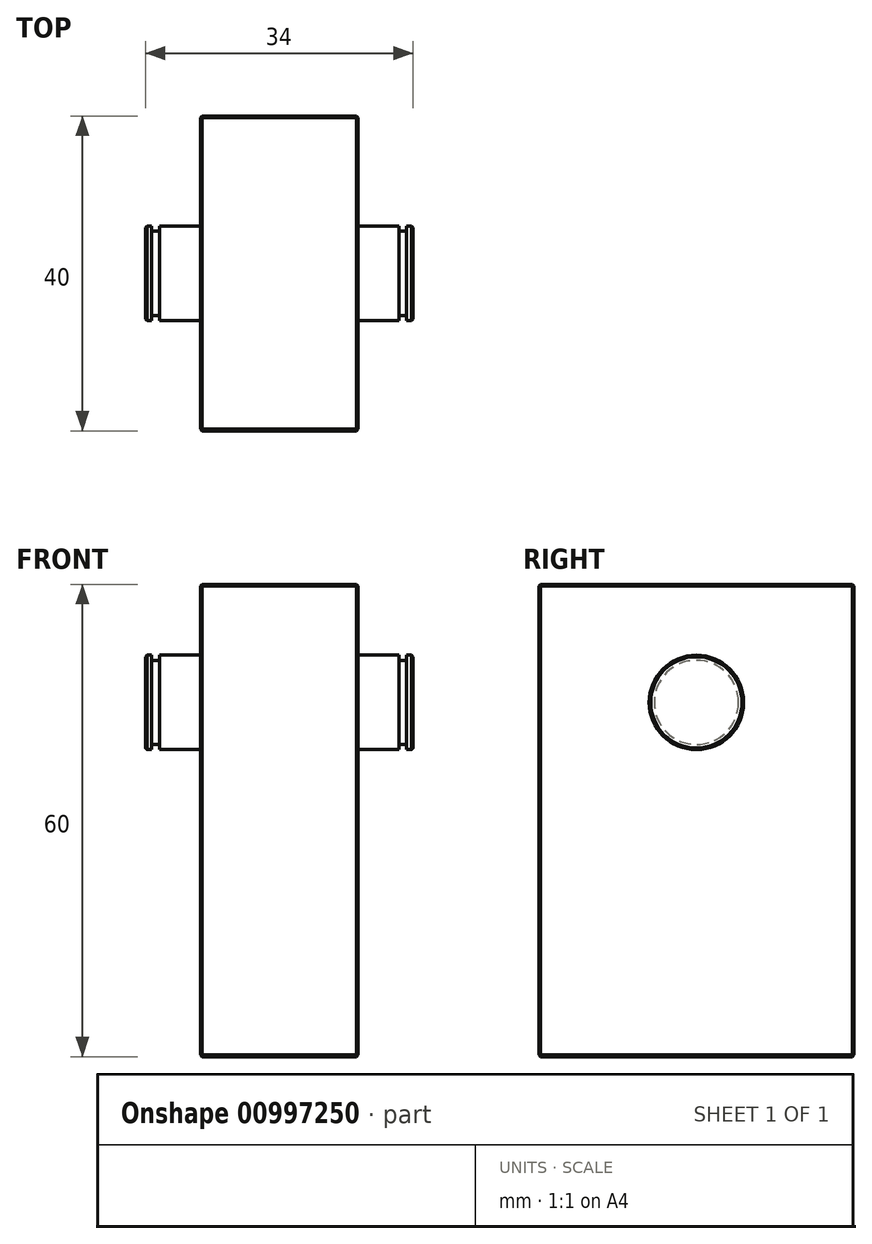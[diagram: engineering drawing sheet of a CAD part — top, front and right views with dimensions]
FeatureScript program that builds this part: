
annotation { "Feature Type Name" : "Feature", "Feature Type Description" : "" }
export const myFeature = defineFeature(function(context is Context, id is Id, definition is map)
    precondition{}
    {
        {
            var Q0;
            Q0=qCreatedBy(makeId("Front.planeOp"),FACE);
            var sketch = newSketch(context, id + "F0", { "sketchPlane" : qUnion([Q0])});
            skLineSegment(sketch, "E0.bottom", {"start": v(-10, 30) * mm, "end": v(10, 30) * mm});
            skLineSegment(sketch, "E0.top", {"start": v(-10, -30) * mm, "end": v(10, -30) * mm});
            skLineSegment(sketch, "E0.left", {"start": v(-10, 30) * mm, "end": v(-10, -30) * mm});
            skLineSegment(sketch, "E0.right", {"start": v(10, 30) * mm, "end": v(10, -30) * mm});
            skSolve(sketch);
        }
        {
            var Q0;
            Q0 = qSketchRegion(id + "F0", true);
            extrude(context, id + "F1", {"entities" : qUnion([Q0]), "depth" : 20 * mm, "offsetDistance" : 25 * mm, "hasSecondDirection" : true, "secondDirectionOppositeDirection" : true, "secondDirectionDepth" : 20 * mm});
        }
        {
            var Q0;
            Q0=makeQuery(id+"F1.opExtrude","SWEPT_EDGE",EDGE,{"disambiguationData":[OSD([sQuery(id+"F0.wireOp",EDGE,"E0.bottom"),sQuery(id+"F0.wireOp",EDGE,"E0.right")])]});
            var Q1;
            Q1=makeQuery(id+"F1.opExtrude","SWEPT_EDGE",EDGE,{"disambiguationData":[OSD([sQuery(id+"F0.wireOp",EDGE,"E0.top"),sQuery(id+"F0.wireOp",EDGE,"E0.left")])]});
            var Q2;
            Q2=makeQuery(id+"F1.opExtrude","SWEPT_EDGE",EDGE,{"disambiguationData":[OSD([sQuery(id+"F0.wireOp",EDGE,"E0.top"),sQuery(id+"F0.wireOp",EDGE,"E0.right")])]});
            var Q3;
            Q3=makeQuery(id+"F1.opExtrude","SWEPT_EDGE",EDGE,{"disambiguationData":[OSD([sQuery(id+"F0.wireOp",EDGE,"E0.bottom"),sQuery(id+"F0.wireOp",EDGE,"E0.left")])]});
            var Q4;
            Q4=makeQuery(id+"F1.opExtrude","CAP_EDGE",EDGE,{"disambiguationData":[OSD([sQuery(id+"F0.wireOp",EDGE,"E0.bottom")])],"isStart":true});
            var Q5;
            Q5=makeQuery(id+"F1.opExtrude","CAP_EDGE",EDGE,{"disambiguationData":[OSD([sQuery(id+"F0.wireOp",EDGE,"E0.bottom")])],"isStart":false});
            var Q6;
            Q6=makeQuery(id+"F1.opExtrude","CAP_EDGE",EDGE,{"disambiguationData":[OSD([sQuery(id+"F0.wireOp",EDGE,"E0.top")])],"isStart":true});
            var Q7;
            Q7=makeQuery(id+"F1.opExtrude","CAP_EDGE",EDGE,{"disambiguationData":[OSD([sQuery(id+"F0.wireOp",EDGE,"E0.top")])],"isStart":false});
            var Q8;
            Q8=makeQuery(id+"F1.opExtrude","CAP_EDGE",EDGE,{"disambiguationData":[OSD([sQuery(id+"F0.wireOp",EDGE,"E0.left")])],"isStart":true});
            var Q9;
            Q9=makeQuery(id+"F1.opExtrude","CAP_EDGE",EDGE,{"disambiguationData":[OSD([sQuery(id+"F0.wireOp",EDGE,"E0.left")])],"isStart":false});
            var Q10;
            Q10=makeQuery(id+"F1.opExtrude","CAP_EDGE",EDGE,{"disambiguationData":[OSD([sQuery(id+"F0.wireOp",EDGE,"E0.right")])],"isStart":true});
            var Q11;
            Q11=makeQuery(id+"F1.opExtrude","CAP_EDGE",EDGE,{"disambiguationData":[OSD([sQuery(id+"F0.wireOp",EDGE,"E0.right")])],"isStart":false});
            chamfer(context, id + "F2", {"entities" : qUnion([Q0, Q1, Q2, Q3, Q4, Q5, Q6, Q7, Q8, Q9, Q10, Q11]), "width" : 0.2 * mm, "tangentPropagation" : true});
        }
        {
            var Q0;
            Q0=qCreatedBy(makeId("Right.planeOp"),FACE);
            var sketch = newSketch(context, id + "F3", { "sketchPlane" : qUnion([Q0])});
            skCircle(sketch, "E1", {"center": v(0, 15) * mm, "radius": 6 * mm});
            skSolve(sketch);
        }
        {
            var Q0;
            Q0 = qSketchRegion(id + "F3", true);
            extrude(context, id + "F4", {"entities" : qUnion([Q0]), "operationType" : NewBodyOperationType.ADD, "depth" : 17 * mm, "offsetDistance" : 25 * mm, "hasSecondDirection" : true, "secondDirectionOppositeDirection" : true, "secondDirectionDepth" : 17 * mm});
        }
        {
            var Q0;
            Q0=makeQuery(id+"F4.boolean.opBoolean","INTERSECT",EDGE,{"derivedFrom":[makeQuery(id+"F1.opExtrude","SWEPT_FACE",FACE,{"disambiguationData":[OSD([sQuery(id+"F0.wireOp",EDGE,"E0.left")])]}),makeQuery(id+"F4.opExtrude","SWEPT_FACE",FACE,{"disambiguationData":[OSD([sQuery(id+"F3.wireOp",EDGE,"E1")])]})]});
            var Q1;
            Q1=makeQuery(id+"F4.boolean.opBoolean","INTERSECT",EDGE,{"derivedFrom":[makeQuery(id+"F1.opExtrude","SWEPT_FACE",FACE,{"disambiguationData":[OSD([sQuery(id+"F0.wireOp",EDGE,"E0.right")])]}),makeQuery(id+"F4.opExtrude","SWEPT_FACE",FACE,{"disambiguationData":[OSD([sQuery(id+"F3.wireOp",EDGE,"E1")])]})]});
            fillet(context, id + "F5", {"entities" : qUnion([Q0, Q1]), "radius" : 0.2 * mm, "tangentPropagation" : true, "allowEdgeOverflow" : false});
        }
        {
            var Q0;
            Q0=makeQuery(id+"F4.opExtrude","CAP_EDGE",EDGE,{"disambiguationData":[OSD([sQuery(id+"F3.wireOp",EDGE,"E1")])],"isStart":true});
            var Q1;
            Q1=makeQuery(id+"F4.opExtrude","CAP_EDGE",EDGE,{"disambiguationData":[OSD([sQuery(id+"F3.wireOp",EDGE,"E1")])],"isStart":false});
            chamfer(context, id + "F6", {"entities" : qUnion([Q0, Q1]), "width" : 0.2 * mm, "tangentPropagation" : true});
        }
        {
            var Q0;
            Q0=makeQuery(id+"F1.opExtrude","SWEPT_FACE",FACE,{"disambiguationData":[OSD([sQuery(id+"F0.wireOp",EDGE,"E0.bottom")])]});
            cPlane(context, id + "F7", {"entities" : qUnion([Q0]), "cplaneType" : CPlaneType.OFFSET, "offset" : 15 * mm, "oppositeDirection" : true, "width" : 150 * mm, "height" : 150 * mm});
        }
        {
            var Q0;
            Q0=qCreatedBy(id+"F7.planeOp",FACE);
            var sketch = newSketch(context, id + "F8", { "sketchPlane" : qUnion([Q0])});
            skLineSegment(sketch, "E2.bottom", {"start": v(-16.2, 6) * mm, "end": v(-15.2, 6) * mm});
            skLineSegment(sketch, "E2.top", {"start": v(-16.2, 5.35) * mm, "end": v(-15.2, 5.35) * mm});
            skLineSegment(sketch, "E2.left", {"start": v(-16.2, 6) * mm, "end": v(-16.2, 5.35) * mm});
            skLineSegment(sketch, "E2.right", {"start": v(-15.2, 6) * mm, "end": v(-15.2, 5.35) * mm});
            skLineSegment(sketch, "E3", {"start": v(0, 15.83) * mm, "end": v(0, -14.06) * mm, "construction": true});
            skLineSegment(sketch, "E4.MirrorCS", {"start": v(15.2, 6) * mm, "end": v(15.2, 5.35) * mm});
            skLineSegment(sketch, "E5.MirrorCS", {"start": v(16.2, 5.35) * mm, "end": v(15.2, 5.35) * mm});
            skLineSegment(sketch, "E6.MirrorCS", {"start": v(16.2, 6) * mm, "end": v(16.2, 5.35) * mm});
            skLineSegment(sketch, "E7.MirrorCS", {"start": v(16.2, 6) * mm, "end": v(15.2, 6) * mm});
            skLineSegment(sketch, "E8", {"start": v(-20.35, 0) * mm, "end": v(22.2, 0) * mm, "construction": true});
            skSolve(sketch);
        }
        {
            var Q0;
            Q0 = qSketchRegion(id + "F8", true);
            var Q1;
            Q1=sQuery(id+"F8.wireOp",EDGE,"E8");
            revolve(context, id + "F9", {"operationType" : NewBodyOperationType.REMOVE, "surfaceOperationType" : NewSurfaceOperationType.NEW, "entities" : qUnion([Q0]), "axis" : qUnion([Q1]), "revolveType" : RevolveType.FULL, "oppositeDirection" : true});
        }
    });
